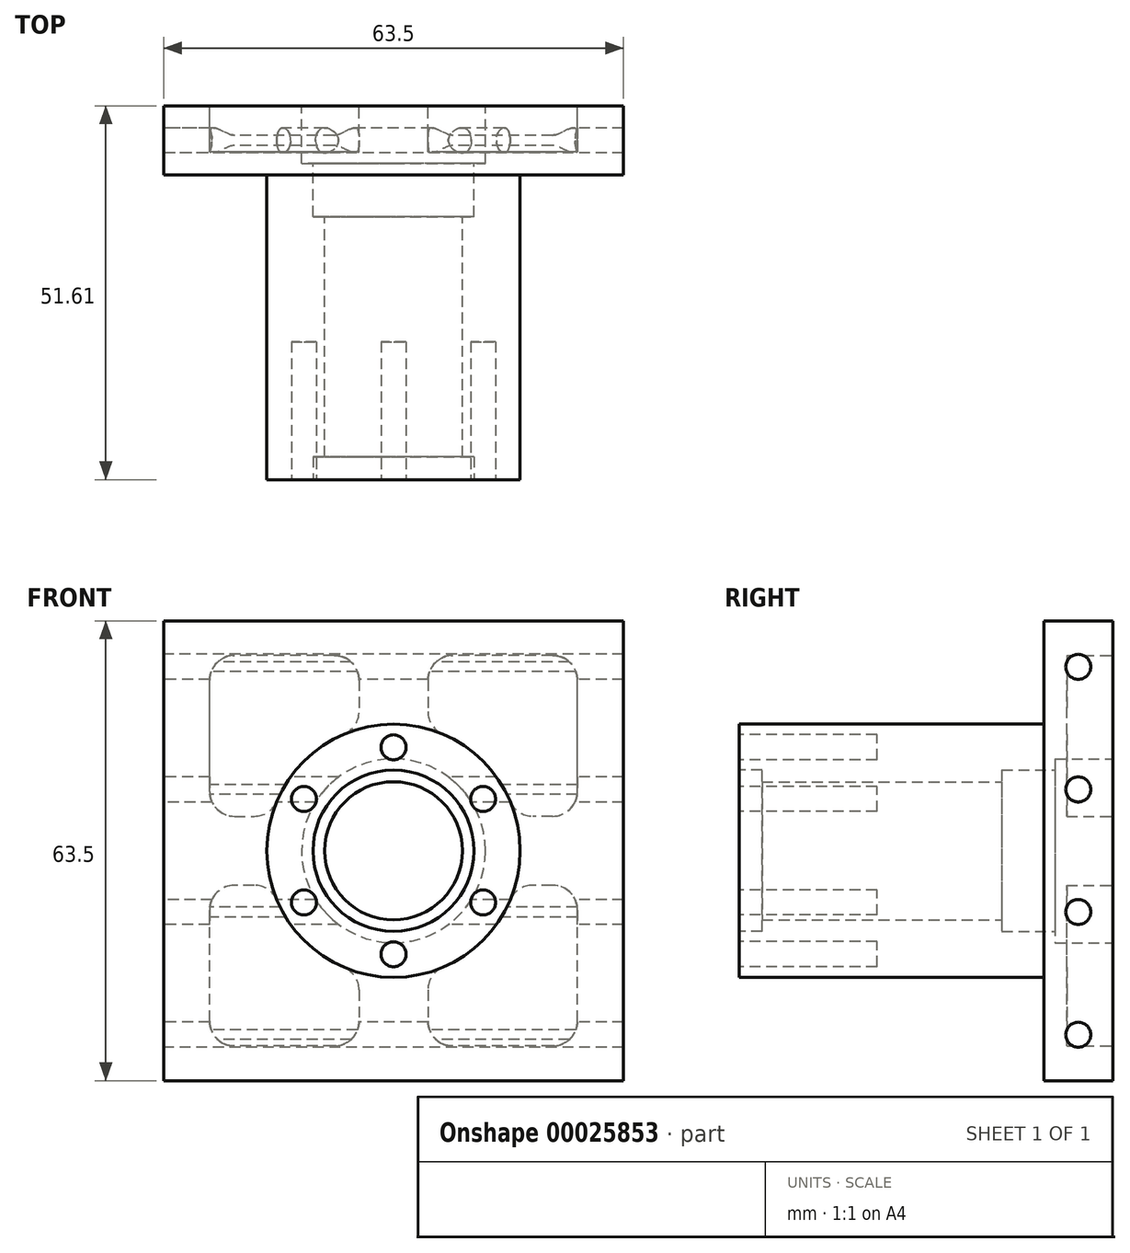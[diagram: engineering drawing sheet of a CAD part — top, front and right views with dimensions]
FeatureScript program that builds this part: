
annotation { "Feature Type Name" : "Feature", "Feature Type Description" : "" }
export const myFeature = defineFeature(function(context is Context, id is Id, definition is map)
    precondition{}
    {
        {
            var Q0;
            Q0=qCreatedBy(makeId("Front.planeOp"),FACE);
            var sketch = newSketch(context, id + "F0", { "sketchPlane" : qUnion([Q0])});
            skLineSegment(sketch, "E0.rect.bottom", {"start": v(31.75, -31.75) * mm, "end": v(-31.75, -31.75) * mm});
            skLineSegment(sketch, "E0.rect.top", {"start": v(31.75, 31.75) * mm, "end": v(-31.75, 31.75) * mm});
            skLineSegment(sketch, "E0.rect.left", {"start": v(31.75, -31.75) * mm, "end": v(31.75, 31.75) * mm});
            skLineSegment(sketch, "E0.rect.right", {"start": v(-31.75, -31.75) * mm, "end": v(-31.75, 31.75) * mm});
            skPoint(sketch, "E0.rect.middle", {"position": v(0, 0) * mm});
            skSolve(sketch);
        }
        {
            var Q0;
            Q0=makeQuery(id+"F0.imprint","IMPRINT",FACE,{"disambiguationData":[TD([[makeQuery(id+"F0.imprint","IMPRINT",EDGE,{"derivedFrom":sQuery(id+"F0.wireOp",EDGE,"E0.rect.bottom")}),-1.0]])]});
            extrude(context, id + "F1", {"entities" : qUnion([Q0]), "depth" : 9.52 * mm});
        }
        {
            var Q0;
            Q0=makeQuery(id+"F1.opExtrude","CAP_FACE",FACE,{"disambiguationData":[OSD([sQuery(id+"F0.wireOp",EDGE,"E0.rect.bottom"),sQuery(id+"F0.wireOp",EDGE,"E0.rect.top"),sQuery(id+"F0.wireOp",EDGE,"E0.rect.left"),sQuery(id+"F0.wireOp",EDGE,"E0.rect.right")])],"isStart":false});
            var sketch = newSketch(context, id + "F2", { "sketchPlane" : qUnion([Q0])});
            skCircle(sketch, "E1", {"center": v(0, 0) * mm, "radius": 17.49 * mm});
            skSolve(sketch);
        }
        {
            var Q0;
            Q0=makeQuery(id+"F2.imprint","IMPRINT",FACE,{"disambiguationData":[TD([[makeQuery(id+"F2.imprint","IMPRINT",EDGE,{"derivedFrom":sQuery(id+"F2.wireOp",EDGE,"E1")}),1.0]])]});
            extrude(context, id + "F3", {"entities" : qUnion([Q0]), "operationType" : NewBodyOperationType.ADD, "depth" : 42.1 * mm});
        }
        {
            var Q0;
            Q0=makeQuery(id+"F3.opExtrude","CAP_FACE",FACE,{"disambiguationData":[OSD([sQuery(id+"F2.wireOp",EDGE,"E1")])],"isStart":false});
            var sketch = newSketch(context, id + "F4", { "sketchPlane" : qUnion([Q0])});
            skCircle(sketch, "E2", {"center": v(0, 0) * mm, "radius": 14.29 * mm, "construction": true});
            skLineSegment(sketch, "E3.0", {"start": v(0, -14.29) * mm, "end": v(-12.37, -7.14) * mm, "construction": true});
            skLineSegment(sketch, "E3.1", {"start": v(-12.37, -7.14) * mm, "end": v(-12.37, 7.14) * mm, "construction": true});
            skLineSegment(sketch, "E3.2", {"start": v(-12.37, 7.14) * mm, "end": v(0, 14.29) * mm, "construction": true});
            skLineSegment(sketch, "E3.3", {"start": v(0, 14.29) * mm, "end": v(12.37, 7.14) * mm, "construction": true});
            skLineSegment(sketch, "E3.4", {"start": v(12.37, 7.14) * mm, "end": v(12.37, -7.14) * mm, "construction": true});
            skLineSegment(sketch, "E3.5", {"start": v(12.37, -7.14) * mm, "end": v(0, -14.29) * mm, "construction": true});
            skCircle(sketch, "E4", {"center": v(-12.37, 7.14) * mm, "radius": 1.73 * mm});
            skCircle(sketch, "E5", {"center": v(0, 14.29) * mm, "radius": 1.73 * mm});
            skCircle(sketch, "E6", {"center": v(12.37, 7.14) * mm, "radius": 1.73 * mm});
            skCircle(sketch, "E7", {"center": v(12.37, -7.14) * mm, "radius": 1.73 * mm});
            skCircle(sketch, "E8", {"center": v(0, -14.29) * mm, "radius": 1.73 * mm});
            skCircle(sketch, "E9", {"center": v(-12.37, -7.14) * mm, "radius": 1.73 * mm});
            skSolve(sketch);
        }
        {
            var Q0;
            Q0=makeQuery(id+"F4.imprint","IMPRINT",FACE,{"disambiguationData":[TD([[makeQuery(id+"F4.imprint","IMPRINT",EDGE,{"derivedFrom":sQuery(id+"F4.wireOp",EDGE,"E5")}),1.0]])]});
            var Q1;
            Q1=makeQuery(id+"F4.imprint","IMPRINT",FACE,{"disambiguationData":[TD([[makeQuery(id+"F4.imprint","IMPRINT",EDGE,{"derivedFrom":sQuery(id+"F4.wireOp",EDGE,"E4")}),1.0]])]});
            var Q2;
            Q2=makeQuery(id+"F4.imprint","IMPRINT",FACE,{"disambiguationData":[TD([[makeQuery(id+"F4.imprint","IMPRINT",EDGE,{"derivedFrom":sQuery(id+"F4.wireOp",EDGE,"E9")}),1.0]])]});
            var Q3;
            Q3=makeQuery(id+"F4.imprint","IMPRINT",FACE,{"disambiguationData":[TD([[makeQuery(id+"F4.imprint","IMPRINT",EDGE,{"derivedFrom":sQuery(id+"F4.wireOp",EDGE,"E8")}),1.0]])]});
            var Q4;
            Q4=makeQuery(id+"F4.imprint","IMPRINT",FACE,{"disambiguationData":[TD([[makeQuery(id+"F4.imprint","IMPRINT",EDGE,{"derivedFrom":sQuery(id+"F4.wireOp",EDGE,"E7")}),1.0]])]});
            var Q5;
            Q5=makeQuery(id+"F4.imprint","IMPRINT",FACE,{"disambiguationData":[TD([[makeQuery(id+"F4.imprint","IMPRINT",EDGE,{"derivedFrom":sQuery(id+"F4.wireOp",EDGE,"E6")}),1.0]])]});
            extrude(context, id + "F5", {"entities" : qUnion([Q0, Q1, Q2, Q3, Q4, Q5]), "operationType" : NewBodyOperationType.REMOVE, "oppositeDirection" : true, "depth" : 19.05 * mm});
        }
        {
            var Q0;
            Q0=makeQuery(id+"F1.opExtrude","CAP_FACE",FACE,{"disambiguationData":[OSD([sQuery(id+"F0.wireOp",EDGE,"E0.rect.bottom"),sQuery(id+"F0.wireOp",EDGE,"E0.rect.top"),sQuery(id+"F0.wireOp",EDGE,"E0.rect.left"),sQuery(id+"F0.wireOp",EDGE,"E0.rect.right")])],"isStart":true});
            var sketch = newSketch(context, id + "F6", { "sketchPlane" : qUnion([Q0])});
            skCircle(sketch, "E10", {"center": v(0, 0) * mm, "radius": 12.7 * mm});
            skSolve(sketch);
        }
        {
            var Q0;
            Q0=makeQuery(id+"F6.imprint","IMPRINT",FACE,{"disambiguationData":[TD([[makeQuery(id+"F6.imprint","IMPRINT",EDGE,{"derivedFrom":sQuery(id+"F6.wireOp",EDGE,"E10")}),1.0]])]});
            extrude(context, id + "F7", {"entities" : qUnion([Q0]), "operationType" : NewBodyOperationType.REMOVE, "oppositeDirection" : true, "depth" : 7.95 * mm});
        }
        {
            var Q0;
            Q0=makeQuery(id+"F7.boolean.opBoolean","COPY",FACE,{"derivedFrom":makeQuery(id+"F7.opExtrude","CAP_FACE",FACE,{"disambiguationData":[OSD([sQuery(id+"F6.wireOp",EDGE,"E10")])],"isStart":false})});
            var sketch = newSketch(context, id + "F8", { "sketchPlane" : qUnion([Q0])});
            skCircle(sketch, "E11", {"center": v(0, 0) * mm, "radius": 11.13 * mm});
            skSolve(sketch);
        }
        {
            var Q0;
            Q0=makeQuery(id+"F8.imprint","IMPRINT",FACE,{"disambiguationData":[TD([[makeQuery(id+"F8.imprint","IMPRINT",EDGE,{"derivedFrom":sQuery(id+"F8.wireOp",EDGE,"E11")}),1.0]])]});
            extrude(context, id + "F9", {"entities" : qUnion([Q0]), "operationType" : NewBodyOperationType.REMOVE, "oppositeDirection" : true, "depth" : 7.37 * mm});
        }
        {
            var Q0;
            Q0=makeQuery(id+"F9.boolean.opBoolean","COPY",FACE,{"derivedFrom":makeQuery(id+"F9.opExtrude","CAP_FACE",FACE,{"disambiguationData":[OSD([sQuery(id+"F8.wireOp",EDGE,"E11")])],"isStart":false})});
            var sketch = newSketch(context, id + "F10", { "sketchPlane" : qUnion([Q0])});
            skCircle(sketch, "E12", {"center": v(0, 0) * mm, "radius": 9.53 * mm});
            skSolve(sketch);
        }
        {
            var Q0;
            Q0=makeQuery(id+"F10.imprint","IMPRINT",FACE,{"disambiguationData":[TD([[makeQuery(id+"F10.imprint","IMPRINT",EDGE,{"derivedFrom":sQuery(id+"F10.wireOp",EDGE,"E12")}),1.0]])]});
            extrude(context, id + "F11", {"entities" : qUnion([Q0]), "operationType" : NewBodyOperationType.REMOVE, "oppositeDirection" : true, "depth" : 33.12 * mm});
        }
        {
            var Q0;
            Q0=makeQuery(id+"F3.opExtrude","CAP_FACE",FACE,{"disambiguationData":[OSD([sQuery(id+"F2.wireOp",EDGE,"E1")])],"isStart":false});
            var sketch = newSketch(context, id + "F12", { "sketchPlane" : qUnion([Q0])});
            skCircle(sketch, "E13", {"center": v(0, 0) * mm, "radius": 11.13 * mm});
            skSolve(sketch);
        }
        {
            var Q0;
            Q0=makeQuery(id+"F12.imprint","IMPRINT",FACE,{"disambiguationData":[TD([[makeQuery(id+"F12.imprint","IMPRINT",EDGE,{"derivedFrom":sQuery(id+"F12.wireOp",EDGE,"E13")}),1.0]])]});
            extrude(context, id + "F13", {"entities" : qUnion([Q0]), "operationType" : NewBodyOperationType.REMOVE, "oppositeDirection" : true, "depth" : 3.17 * mm});
        }
        {
            var Q0;
            Q0=makeQuery(id+"F1.opExtrude","SWEPT_FACE",FACE,{"disambiguationData":[OSD([sQuery(id+"F0.wireOp",EDGE,"E0.rect.right")])]});
            var sketch = newSketch(context, id + "F14", { "sketchPlane" : qUnion([Q0])});
            skLineSegment(sketch, "E14", {"start": v(4.76, 31.75) * mm, "end": v(4.76, -31.75) * mm, "construction": true});
            skCircle(sketch, "E15", {"center": v(4.76, 25.4) * mm, "radius": 1.73 * mm});
            skCircle(sketch, "E16", {"center": v(4.76, 8.46) * mm, "radius": 1.73 * mm});
            skCircle(sketch, "E17", {"center": v(4.76, -8.46) * mm, "radius": 1.73 * mm});
            skCircle(sketch, "E18", {"center": v(4.76, -25.4) * mm, "radius": 1.73 * mm});
            skSolve(sketch);
        }
        {
            var Q0;
            Q0=makeQuery(id+"F1.opExtrude","CAP_FACE",FACE,{"disambiguationData":[OSD([sQuery(id+"F0.wireOp",EDGE,"E0.rect.bottom"),sQuery(id+"F0.wireOp",EDGE,"E0.rect.top"),sQuery(id+"F0.wireOp",EDGE,"E0.rect.left"),sQuery(id+"F0.wireOp",EDGE,"E0.rect.right")])],"isStart":true});
            var sketch = newSketch(context, id + "F15", { "sketchPlane" : qUnion([Q0])});
            skLineSegment(sketch, "E19.rect.bottom", {"start": v(25.4, -26.97) * mm, "end": v(4.76, -26.97) * mm});
            skLineSegment(sketch, "E19.rect.top", {"start": v(25.4, 26.97) * mm, "end": v(4.76, 26.97) * mm});
            skLineSegment(sketch, "E19.rect.left", {"start": v(25.4, -26.97) * mm, "end": v(25.4, -4.76) * mm});
            skLineSegment(sketch, "E19.rect.right", {"start": v(-25.4, -26.97) * mm, "end": v(-25.4, -4.76) * mm});
            skPoint(sketch, "E19.rect.middle", {"position": v(0, 0) * mm});
            skArc(sketch, "E20", {"start": v(-4.76, 16.81) * mm, "mid": v(-12.36, 12.36) * mm, "end": v(-16.81, 4.76) * mm});
            skLineSegment(sketch, "E21", {"start": v(0, 26.97) * mm, "end": v(0, -26.97) * mm, "construction": true});
            skLineSegment(sketch, "E22", {"start": v(-25.4, 0) * mm, "end": v(25.4, 0) * mm, "construction": true});
            skLineSegment(sketch, "E23", {"start": v(-4.76, 26.97) * mm, "end": v(-4.76, 16.81) * mm});
            skLineSegment(sketch, "E24", {"start": v(4.76, 26.97) * mm, "end": v(4.76, 16.81) * mm});
            skLineSegment(sketch, "E25", {"start": v(25.4, 4.76) * mm, "end": v(16.81, 4.76) * mm});
            skLineSegment(sketch, "E26", {"start": v(16.81, -4.76) * mm, "end": v(25.4, -4.76) * mm});
            skLineSegment(sketch, "E27", {"start": v(4.76, -16.81) * mm, "end": v(4.76, -26.97) * mm});
            skLineSegment(sketch, "E28", {"start": v(-4.76, -16.81) * mm, "end": v(-4.76, -26.97) * mm});
            skLineSegment(sketch, "E29", {"start": v(-25.4, 4.76) * mm, "end": v(-16.81, 4.76) * mm});
            skLineSegment(sketch, "E30", {"start": v(-25.4, -4.76) * mm, "end": v(-16.81, -4.76) * mm});
            skLineSegment(sketch, "E31.trimOffspring", {"start": v(-4.76, 26.97) * mm, "end": v(-25.4, 26.97) * mm});
            skLineSegment(sketch, "E32.trimOffspring", {"start": v(25.4, 4.76) * mm, "end": v(25.4, 26.97) * mm});
            skArc(sketch, "E33.trimOffspring", {"start": v(16.81, 4.76) * mm, "mid": v(12.36, 12.36) * mm, "end": v(4.76, 16.81) * mm});
            skLineSegment(sketch, "E34.trimOffspring", {"start": v(-4.76, -26.97) * mm, "end": v(-25.4, -26.97) * mm});
            skArc(sketch, "E35.trimOffspring", {"start": v(4.76, -16.81) * mm, "mid": v(12.36, -12.36) * mm, "end": v(16.81, -4.76) * mm});
            skArc(sketch, "E36.trimOffspring", {"start": v(-16.81, -4.76) * mm, "mid": v(-12.36, -12.36) * mm, "end": v(-4.76, -16.81) * mm});
            skLineSegment(sketch, "E37.trimOffspring", {"start": v(-25.4, 4.76) * mm, "end": v(-25.4, 26.97) * mm});
            skSolve(sketch);
        }
        {
            var Q0;
            {var subQ1=sQuery(id+"F15.wireOp",EDGE,"E23");Q0=makeQuery(id+"F15.imprint","IMPRINT",FACE,{"disambiguationData":[TD([[makeQuery(id+"F15.imprint","IMPRINT",EDGE,{"derivedFrom":subQ1}),-1.0]])]});}
            var Q1;
            {var subQ1=sQuery(id+"F15.wireOp",EDGE,"E24");Q1=makeQuery(id+"F15.imprint","IMPRINT",FACE,{"disambiguationData":[TD([[makeQuery(id+"F15.imprint","IMPRINT",EDGE,{"derivedFrom":subQ1}),1.0]])]});}
            var Q2;
            {var subQ2=sQuery(id+"F15.wireOp",EDGE,"E26");Q2=makeQuery(id+"F15.imprint","IMPRINT",FACE,{"disambiguationData":[TD([[makeQuery(id+"F15.imprint","IMPRINT",EDGE,{"derivedFrom":subQ2}),-1.0]])]});}
            var Q3;
            {var subQ1=sQuery(id+"F15.wireOp",EDGE,"E28");Q3=makeQuery(id+"F15.imprint","IMPRINT",FACE,{"disambiguationData":[TD([[makeQuery(id+"F15.imprint","IMPRINT",EDGE,{"derivedFrom":subQ1}),-1.0]])]});}
            extrude(context, id + "F16", {"entities" : qUnion([Q0, Q1, Q2, Q3]), "operationType" : NewBodyOperationType.REMOVE, "oppositeDirection" : true, "depth" : 6.35 * mm});
        }
        {
            var Q0;
            Q0=makeQuery(id+"F16.boolean.opBoolean","COPY",EDGE,{"derivedFrom":makeQuery(id+"F16.opExtrude","SWEPT_EDGE",EDGE,{"disambiguationData":[OSD([sQuery(id+"F15.wireOp",EDGE,"E19.rect.right"),sQuery(id+"F15.wireOp",EDGE,"E30")])]})});
            var Q1;
            Q1=makeQuery(id+"F16.boolean.opBoolean","COPY",EDGE,{"derivedFrom":makeQuery(id+"F16.opExtrude","SWEPT_EDGE",EDGE,{"disambiguationData":[OSD([sQuery(id+"F15.wireOp",EDGE,"E30"),sQuery(id+"F15.wireOp",EDGE,"E36.trimOffspring")])]})});
            var Q2;
            Q2=makeQuery(id+"F16.boolean.opBoolean","COPY",EDGE,{"derivedFrom":makeQuery(id+"F16.opExtrude","SWEPT_EDGE",EDGE,{"disambiguationData":[OSD([sQuery(id+"F15.wireOp",EDGE,"E28"),sQuery(id+"F15.wireOp",EDGE,"E36.trimOffspring")])]})});
            var Q3;
            Q3=makeQuery(id+"F16.boolean.opBoolean","COPY",EDGE,{"derivedFrom":makeQuery(id+"F16.opExtrude","SWEPT_EDGE",EDGE,{"disambiguationData":[OSD([sQuery(id+"F15.wireOp",EDGE,"E28"),sQuery(id+"F15.wireOp",EDGE,"E34.trimOffspring")])]})});
            var Q4;
            Q4=makeQuery(id+"F16.boolean.opBoolean","COPY",EDGE,{"derivedFrom":makeQuery(id+"F16.opExtrude","SWEPT_EDGE",EDGE,{"disambiguationData":[OSD([sQuery(id+"F15.wireOp",EDGE,"E19.rect.right"),sQuery(id+"F15.wireOp",EDGE,"E34.trimOffspring")])]})});
            var Q5;
            Q5=makeQuery(id+"F16.boolean.opBoolean","COPY",EDGE,{"derivedFrom":makeQuery(id+"F16.opExtrude","SWEPT_EDGE",EDGE,{"disambiguationData":[OSD([sQuery(id+"F15.wireOp",EDGE,"E26"),sQuery(id+"F15.wireOp",EDGE,"E35.trimOffspring")])]})});
            var Q6;
            Q6=makeQuery(id+"F16.boolean.opBoolean","COPY",EDGE,{"derivedFrom":makeQuery(id+"F16.opExtrude","SWEPT_EDGE",EDGE,{"disambiguationData":[OSD([sQuery(id+"F15.wireOp",EDGE,"E19.rect.left"),sQuery(id+"F15.wireOp",EDGE,"E26")])]})});
            var Q7;
            Q7=makeQuery(id+"F16.boolean.opBoolean","COPY",EDGE,{"derivedFrom":makeQuery(id+"F16.opExtrude","SWEPT_EDGE",EDGE,{"disambiguationData":[OSD([sQuery(id+"F15.wireOp",EDGE,"E19.rect.bottom"),sQuery(id+"F15.wireOp",EDGE,"E19.rect.left")])]})});
            var Q8;
            Q8=makeQuery(id+"F16.boolean.opBoolean","COPY",EDGE,{"derivedFrom":makeQuery(id+"F16.opExtrude","SWEPT_EDGE",EDGE,{"disambiguationData":[OSD([sQuery(id+"F15.wireOp",EDGE,"E19.rect.bottom"),sQuery(id+"F15.wireOp",EDGE,"E27")])]})});
            var Q9;
            Q9=makeQuery(id+"F16.boolean.opBoolean","COPY",EDGE,{"derivedFrom":makeQuery(id+"F16.opExtrude","SWEPT_EDGE",EDGE,{"disambiguationData":[OSD([sQuery(id+"F15.wireOp",EDGE,"E27"),sQuery(id+"F15.wireOp",EDGE,"E35.trimOffspring")])]})});
            var Q10;
            Q10=makeQuery(id+"F16.boolean.opBoolean","COPY",EDGE,{"derivedFrom":makeQuery(id+"F16.opExtrude","SWEPT_EDGE",EDGE,{"disambiguationData":[OSD([sQuery(id+"F15.wireOp",EDGE,"E25"),sQuery(id+"F15.wireOp",EDGE,"E33.trimOffspring")])]})});
            var Q11;
            Q11=makeQuery(id+"F16.boolean.opBoolean","COPY",EDGE,{"derivedFrom":makeQuery(id+"F16.opExtrude","SWEPT_EDGE",EDGE,{"disambiguationData":[OSD([sQuery(id+"F15.wireOp",EDGE,"E25"),sQuery(id+"F15.wireOp",EDGE,"E32.trimOffspring")])]})});
            var Q12;
            Q12=makeQuery(id+"F16.boolean.opBoolean","COPY",EDGE,{"derivedFrom":makeQuery(id+"F16.opExtrude","SWEPT_EDGE",EDGE,{"disambiguationData":[OSD([sQuery(id+"F15.wireOp",EDGE,"E19.rect.top"),sQuery(id+"F15.wireOp",EDGE,"E32.trimOffspring")])]})});
            var Q13;
            Q13=makeQuery(id+"F16.boolean.opBoolean","COPY",EDGE,{"derivedFrom":makeQuery(id+"F16.opExtrude","SWEPT_EDGE",EDGE,{"disambiguationData":[OSD([sQuery(id+"F15.wireOp",EDGE,"E19.rect.top"),sQuery(id+"F15.wireOp",EDGE,"E24")])]})});
            var Q14;
            Q14=makeQuery(id+"F16.boolean.opBoolean","COPY",EDGE,{"derivedFrom":makeQuery(id+"F16.opExtrude","SWEPT_EDGE",EDGE,{"disambiguationData":[OSD([sQuery(id+"F15.wireOp",EDGE,"E24"),sQuery(id+"F15.wireOp",EDGE,"E33.trimOffspring")])]})});
            var Q15;
            Q15=makeQuery(id+"F16.boolean.opBoolean","COPY",EDGE,{"derivedFrom":makeQuery(id+"F16.opExtrude","SWEPT_EDGE",EDGE,{"disambiguationData":[OSD([sQuery(id+"F15.wireOp",EDGE,"E31.trimOffspring"),sQuery(id+"F15.wireOp",EDGE,"E37.trimOffspring")])]})});
            var Q16;
            Q16=makeQuery(id+"F16.boolean.opBoolean","COPY",EDGE,{"derivedFrom":makeQuery(id+"F16.opExtrude","SWEPT_EDGE",EDGE,{"disambiguationData":[OSD([sQuery(id+"F15.wireOp",EDGE,"E29"),sQuery(id+"F15.wireOp",EDGE,"E37.trimOffspring")])]})});
            var Q17;
            Q17=makeQuery(id+"F16.boolean.opBoolean","COPY",EDGE,{"derivedFrom":makeQuery(id+"F16.opExtrude","SWEPT_EDGE",EDGE,{"disambiguationData":[OSD([sQuery(id+"F15.wireOp",EDGE,"E20"),sQuery(id+"F15.wireOp",EDGE,"E29")])]})});
            var Q18;
            Q18=makeQuery(id+"F16.boolean.opBoolean","COPY",EDGE,{"derivedFrom":makeQuery(id+"F16.opExtrude","SWEPT_EDGE",EDGE,{"disambiguationData":[OSD([sQuery(id+"F15.wireOp",EDGE,"E20"),sQuery(id+"F15.wireOp",EDGE,"E23")])]})});
            var Q19;
            Q19=makeQuery(id+"F16.boolean.opBoolean","COPY",EDGE,{"derivedFrom":makeQuery(id+"F16.opExtrude","SWEPT_EDGE",EDGE,{"disambiguationData":[OSD([sQuery(id+"F15.wireOp",EDGE,"E23"),sQuery(id+"F15.wireOp",EDGE,"E31.trimOffspring")])]})});
            fillet(context, id + "F17", {"entities" : qUnion([Q0, Q1, Q2, Q3, Q4, Q5, Q6, Q7, Q8, Q9, Q10, Q11, Q12, Q13, Q14, Q15, Q16, Q17, Q18, Q19]), "radius" : 3.43 * mm, "tangentPropagation" : true, "allowEdgeOverflow" : false});
        }
        {
            var Q0;
            Q0 = qSketchRegion(id + "F14", true);
            extrude(context, id + "F18", {"entities" : qUnion([Q0]), "operationType" : NewBodyOperationType.REMOVE, "endBound" : BoundingType.THROUGH_ALL, "oppositeDirection" : true, "depth" : 25.4 * mm});
        }
    });
